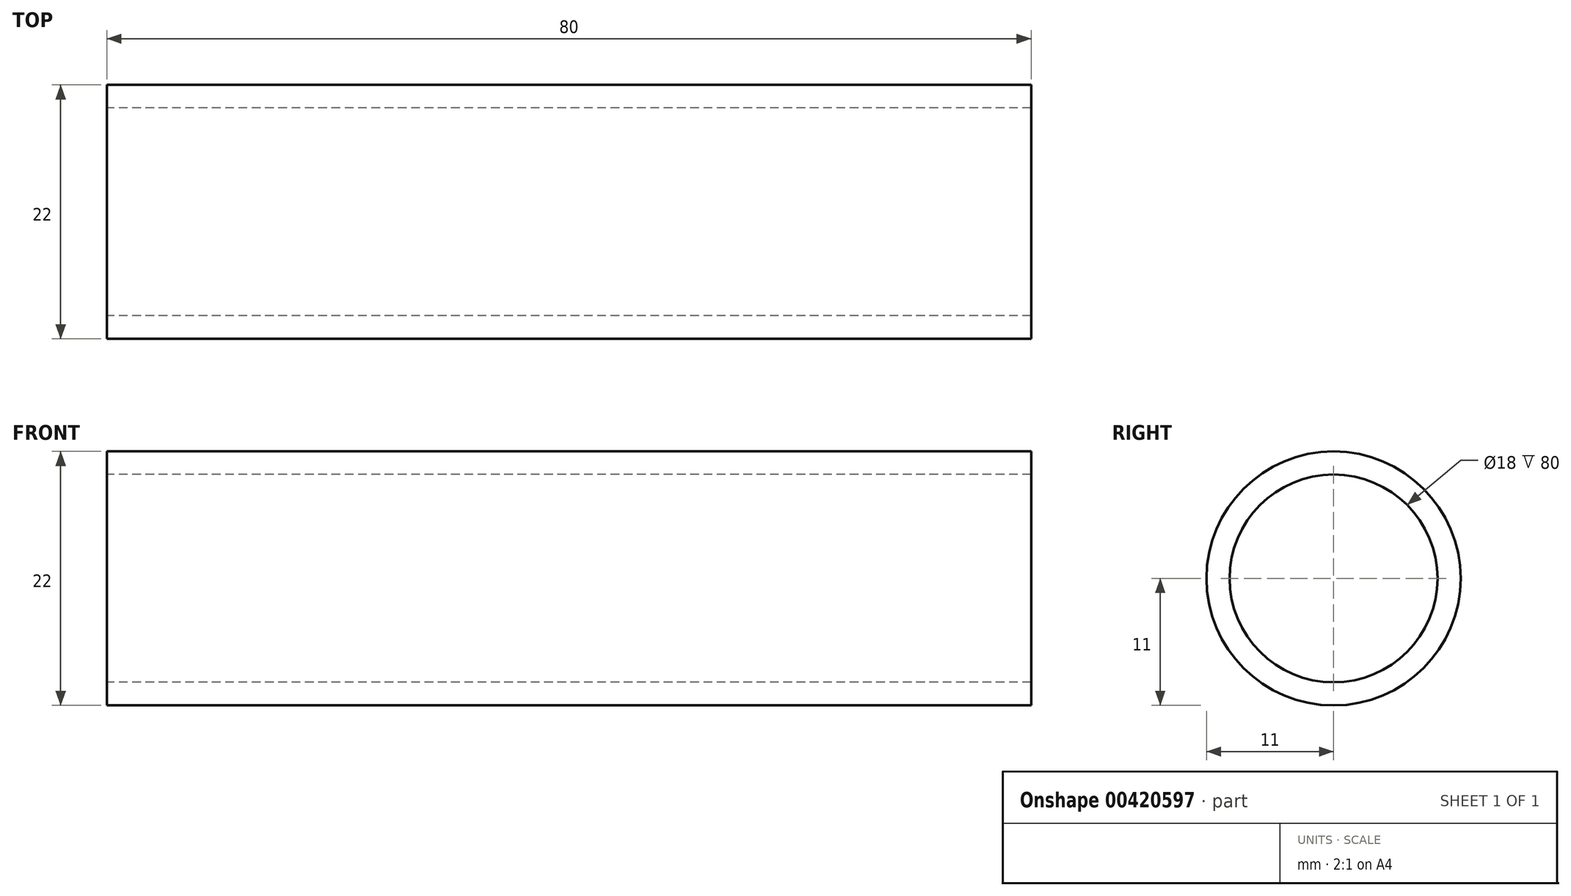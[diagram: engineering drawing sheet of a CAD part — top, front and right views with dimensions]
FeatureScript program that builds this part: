
annotation { "Feature Type Name" : "Feature", "Feature Type Description" : "" }
export const myFeature = defineFeature(function(context is Context, id is Id, definition is map)
    precondition{}
    {
        {
            var Q0;
            Q0=qCreatedBy(makeId("Right.planeOp"),FACE);
            var sketch = newSketch(context, id + "F0", { "sketchPlane" : qUnion([Q0])});
            skCircle(sketch, "E0", {"center": v(0, 0) * mm, "radius": 9 * mm});
            skCircle(sketch, "E1", {"center": v(0, 0) * mm, "radius": 11 * mm});
            skSolve(sketch);
        }
        {
            var Q0;
            Q0 = qSketchRegion(id + "F0", true);
            extrude(context, id + "F1", {"entities" : qUnion([Q0]), "depth" : 80 * mm, "offsetDistance" : 25 * mm, "symmetric" : true});
        }
    });
